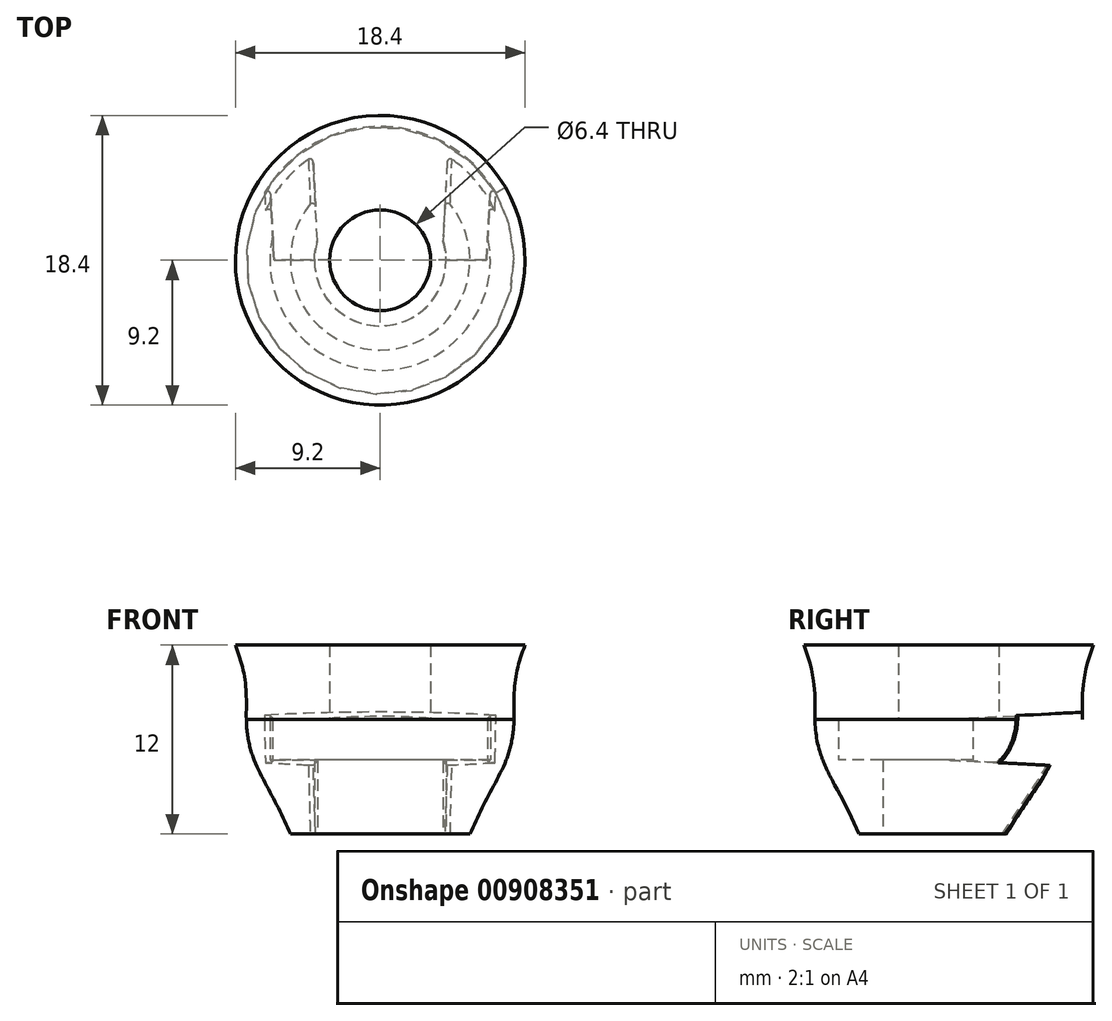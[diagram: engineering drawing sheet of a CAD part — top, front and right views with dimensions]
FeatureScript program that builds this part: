
annotation { "Feature Type Name" : "Feature", "Feature Type Description" : "" }
export const myFeature = defineFeature(function(context is Context, id is Id, definition is map)
    precondition{}
    {
        {
            var Q0;
            Q0=qCreatedBy(makeId("Front.planeOp"),FACE);
            var sketch = newSketch(context, id + "F0", { "sketchPlane" : qUnion([Q0])});
            skLineSegment(sketch, "E0.bottom", {"start": v(0, 6) * mm, "end": v(-3.2, 6) * mm});
            skLineSegment(sketch, "E0.top", {"start": v(3.2, -6) * mm, "end": v(-3.2, -6) * mm});
            skLineSegment(sketch, "E0.left", {"start": v(3.2, 6) * mm, "end": v(3.2, 1.3) * mm});
            skLineSegment(sketch, "E0.right", {"start": v(-3.2, 6) * mm, "end": v(-3.2, -6) * mm});
            skPoint(sketch, "E0.middle", {"position": v(0, 0) * mm});
            skLineSegment(sketch, "E1", {"start": v(3.2, -6) * mm, "end": v(5.7, -6) * mm});
            skLineSegment(sketch, "E2.bottom", {"start": v(7, 1.3) * mm, "end": v(3.2, 1.3) * mm});
            skLineSegment(sketch, "E2.top", {"start": v(7, -1.3) * mm, "end": v(3.2, -1.3) * mm});
            skLineSegment(sketch, "E2.left", {"start": v(7, 1.3) * mm, "end": v(7, -1.3) * mm});
            skLineSegment(sketch, "E2.right", {"start": v(-7, 1.3) * mm, "end": v(-7, -1.3) * mm});
            skLineSegment(sketch, "E3", {"start": v(3.2, 6) * mm, "end": v(9.2, 6) * mm});
            skLineSegment(sketch, "E4", {"start": v(7, 1.3) * mm, "end": v(8.5, 1.3) * mm});
            skLineSegment(sketch, "E5", {"start": v(7, -1.3) * mm, "end": v(8, -1.3) * mm});
            skFitSpline(sketch, "E6", {"points": [v(5.7, -6) * mm, v(8, -1.3) * mm, v(8.5, 1.3) * mm, v(9.2, 6) * mm], "startDerivative": vector(7.89, 18.37) * mm, "endDerivative": vector(7.4, 18.45) * mm});
            skLineSegment(sketch, "E7", {"start": v(0, -6) * mm, "end": v(0, 6) * mm});
            skLineSegment(sketch, "E8.trimOffspring", {"start": v(0, 1.3) * mm, "end": v(-7, 1.3) * mm});
            skLineSegment(sketch, "E9.trimOffspring", {"start": v(0, -1.3) * mm, "end": v(-7, -1.3) * mm});
            skLineSegment(sketch, "E10.bottom", {"start": v(-4.17, -1.3) * mm, "end": v(0, -1.3) * mm});
            skLineSegment(sketch, "E10.top", {"start": v(-4.17, -10.7) * mm, "end": v(4.18, -10.7) * mm});
            skLineSegment(sketch, "E10.left", {"start": v(-4.17, -1.3) * mm, "end": v(-4.17, -10.7) * mm});
            skLineSegment(sketch, "E10.right", {"start": v(4.18, -1.3) * mm, "end": v(4.18, -6) * mm});
            skPoint(sketch, "E10.middle", {"position": v(0, -6) * mm});
            skLineSegment(sketch, "E11", {"start": v(4.18, -6) * mm, "end": v(3.2, -6) * mm});
            skLineSegment(sketch, "E12.trimOffspring", {"start": v(3.2, -1.3) * mm, "end": v(4.18, -1.3) * mm});
            skLineSegment(sketch, "E13.trimOffspring", {"start": v(0, -6) * mm, "end": v(-4.17, -6) * mm});
            skSolve(sketch);
        }
        {
            var Q0;
            Q0=makeQuery(id+"F0.imprint","IMPRINT",FACE,{"disambiguationData":[TD([[makeQuery(id+"F0.imprint","IMPRINT",EDGE,{"derivedFrom":sQuery(id+"F0.wireOp",EDGE,"E0.left")}),1.0]])]});
            var Q1;
            Q1=makeQuery(id+"F0.imprint","IMPRINT",FACE,{"disambiguationData":[TD([[makeQuery(id+"F0.imprint","IMPRINT",EDGE,{"derivedFrom":sQuery(id+"F0.wireOp",EDGE,"E2.left")}),1.0]])]});
            var Q2;
            {var subQ1=sQuery(id+"F0.wireOp",EDGE,"E1");Q2=makeQuery(id+"F0.imprint","IMPRINT",FACE,{"disambiguationData":[TD([[makeQuery(id+"F0.imprint","IMPRINT",EDGE,{"derivedFrom":subQ1}),1.0]])]});}
            var Q3;
            Q3=sQuery(id+"F0.wireOp",EDGE,"E7");
            revolve(context, id + "F1", {"surfaceOperationType" : NewSurfaceOperationType.NEW, "entities" : qUnion([Q0, Q1, Q2]), "axis" : qUnion([Q3]), "revolveType" : RevolveType.FULL});
        }
        {
            var Q0;
            Q0=qCreatedBy(makeId("Front.planeOp"),FACE);
            var sketch = newSketch(context, id + "F2", { "sketchPlane" : qUnion([Q0])});
            skLineSegment(sketch, "E14.bottom", {"start": v(-3.93, -10) * mm, "end": v(3.92, -10) * mm});
            skLineSegment(sketch, "E14.top", {"start": v(-3.92, 10) * mm, "end": v(3.93, 10) * mm});
            skLineSegment(sketch, "E14.left", {"start": v(-3.93, -10) * mm, "end": v(-3.92, 1.3) * mm});
            skLineSegment(sketch, "E14.right", {"start": v(3.92, -10) * mm, "end": v(3.92, 10) * mm});
            skPoint(sketch, "E14.middle", {"position": v(0, 0) * mm});
            skLineSegment(sketch, "E15.bottom", {"start": v(-6.75, -1.3) * mm, "end": v(6.75, -1.3) * mm});
            skLineSegment(sketch, "E15.top", {"start": v(-6.75, 1.3) * mm, "end": v(6.75, 1.3) * mm});
            skLineSegment(sketch, "E15.left", {"start": v(-6.75, -1.3) * mm, "end": v(-6.75, 1.3) * mm});
            skLineSegment(sketch, "E15.right", {"start": v(6.75, -1.3) * mm, "end": v(6.75, 1.3) * mm});
            skSolve(sketch);
        }
        {
            var Q0;
            Q0 = qSketchRegion(id + "F2", true);
            extrude(context, id + "F3", {"entities" : qUnion([Q0]), "operationType" : NewBodyOperationType.REMOVE, "oppositeDirection" : true, "depth" : 15 * mm, "offsetDistance" : 25 * mm, "hasDraft" : true, "draftAngle" : 3 * degree});
        }
        {
            var Q0;
            Q0=makeQuery(id+"F3.boolean.opBoolean","INTERSECT",EDGE,{"derivedFrom":[makeQuery(id+"F1.opRevolve","SWEPT_FACE",FACE,{"disambiguationData":[OSD([sQuery(id+"F0.wireOp",EDGE,"E6")])]}),makeQuery(id+"F3.opExtrude","SWEPT_FACE",FACE,{"disambiguationData":[OSD([sQuery(id+"F2.wireOp",EDGE,"E14.left")])]})]});
            var Q1;
            Q1=makeQuery(id+"F3.boolean.opBoolean","INTERSECT",EDGE,{"derivedFrom":[makeQuery(id+"F1.opRevolve","SWEPT_FACE",FACE,{"disambiguationData":[OSD([sQuery(id+"F0.wireOp",EDGE,"E10.right")])]}),makeQuery(id+"F3.opExtrude","SWEPT_FACE",FACE,{"disambiguationData":[OSD([sQuery(id+"F2.wireOp",EDGE,"E14.left")])]})]});
            var Q2;
            Q2=makeQuery(id+"F3.boolean.opBoolean","INTERSECT",EDGE,{"derivedFrom":[makeQuery(id+"F1.opRevolve","SWEPT_FACE",FACE,{"disambiguationData":[OSD([sQuery(id+"F0.wireOp",EDGE,"E10.right")])]}),makeQuery(id+"F3.opExtrude","SWEPT_FACE",FACE,{"disambiguationData":[OSD([sQuery(id+"F2.wireOp",EDGE,"E14.right")])]})]});
            var Q3;
            Q3=makeQuery(id+"F3.boolean.opBoolean","INTERSECT",EDGE,{"derivedFrom":[makeQuery(id+"F1.opRevolve","SWEPT_FACE",FACE,{"disambiguationData":[OSD([sQuery(id+"F0.wireOp",EDGE,"E6")])]}),makeQuery(id+"F3.opExtrude","SWEPT_FACE",FACE,{"disambiguationData":[OSD([sQuery(id+"F2.wireOp",EDGE,"E14.right")])]})]});
            var Q4;
            Q4=makeQuery(id+"F3.boolean.opBoolean","INTERSECT",EDGE,{"derivedFrom":[makeQuery(id+"F1.opRevolve","SWEPT_FACE",FACE,{"disambiguationData":[OSD([sQuery(id+"F0.wireOp",EDGE,"E6")])]}),makeQuery(id+"F3.opExtrude","SWEPT_FACE",FACE,{"disambiguationData":[OSD([sQuery(id+"F2.wireOp",EDGE,"E15.left")])]})]});
            var Q5;
            Q5=makeQuery(id+"F3.boolean.opBoolean","INTERSECT",EDGE,{"derivedFrom":[makeQuery(id+"F1.opRevolve","SWEPT_FACE",FACE,{"disambiguationData":[OSD([sQuery(id+"F0.wireOp",EDGE,"E6")])]}),makeQuery(id+"F3.opExtrude","SWEPT_FACE",FACE,{"disambiguationData":[OSD([sQuery(id+"F2.wireOp",EDGE,"E15.right")])]})]});
            fillet(context, id + "F4", {"entities" : qUnion([Q0, Q1, Q2, Q3, Q4, Q5]), "radius" : 0.2 * mm, "tangentPropagation" : true, "allowEdgeOverflow" : false});
        }
    });
